# Revit family: Diffuser-Carnes-T_Bar_Mount-1-Slot-DTAB
name_source: partatom
category: Duct Accessories
revit_build: Autodesk Revit MEP 2014 (Build: 20130308_1515(x64)
units: mm (PartAtom-declared; Revit-internal decimal feet)

## types (1)
- See Type Catalog
    B Radius = 63"
    Box Length = 23 1/2"
    Catalog = http://www.carnes.com
    D Depth = 2 3/4"
    Default Elevation = 0"
    Depth = 2 3/4"
    Description = Extruded Aluminum 1 Slot Diffuser T-Bar Mount
    Flow = 0 CFM
    Height = 9 1/16"
    Inlet Nominal Size Height D = 3 1/2"
    Inlet Nominal Size Width = 5 1/8"
    Inlet Offset = 10 1/2"
    Inlet Width = 60"
    Length = 24"
    Manufacturer = CARNES COMPANY
    Model = DTAB
    Product Page URL = http://www.carnes.com
    Profile Depth = 5 97/128"
    Revit Object Download Link = http://library.smartbim.com
    Specification Sheet = http://www.carnes.com
    Subcatagory = Air Distribution
    Supply Connection = Diffuser Supply Connector
    Supply Connector = Yes
    URL = http://www.carnes.com
    Unit = Metal - Carnes - Steel Galvanized

## geometry (parser evidence)
native form markers: Blend x2, Sweep x7
no freeform markers — native parametric forms only
